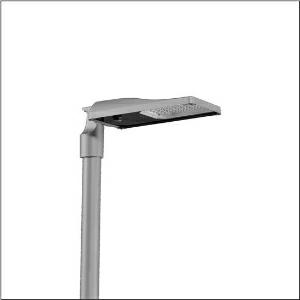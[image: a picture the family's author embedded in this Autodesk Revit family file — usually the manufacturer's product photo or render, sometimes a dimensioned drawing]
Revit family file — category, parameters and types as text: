
# Revit family: streetlight_sl_31_mini___st1_0a_5xh6d3ar08ga_0704
name_source: partatom
category: Lighting Fixtures
units: mm (PartAtom-declared; Revit-internal decimal feet)

## family parameters
Cut with Voids When Loaded = No
Host = Face
Light Source = No
Part Type = Normal
Room Calculation Point = No
Round Connector Dimension = Use Diameter
Shared = No

## types (1)
- --- (1 x LED, 5880 lm, 39.3 W, 3000K)
    Apparent Load = 39 VA
    CIE Flux Codes = 37 72 97 100 100
    Color Rendering = 70
    Color Temperature = 3000K
    Default Elevation = 1800 mm
    Description = Streetlight SL 31 mini D4i mast luminaire for post-top, side-entry; light control with lens of PMMA; light distribution: ST1.0a, direct asymmetric distribution, for standard-compliant lighting for roads and squares; LED: luminous flux: 5.880lm, light colour: 730, colour temperature: 3000K; luminous efficacy: 149,6lm/W; control: pre-setting: logarithmic dimming characteristic, flexible luminous flux parameterisation, time-dependent luminous flux control, constant luminous flux control, power reduction, intelligent temperature release in ECG and LED module, overheat protection; luminaire housing, of diecast aluminium, SITECO metallic grey (DB 702S), corrosivity category C5 high according to DIN EN ISO 12944; cover of toughened safety glass, transparent, opened without tools; mast flange of diecast aluminium, SITECO metallic grey (DB 702S), spigot size: 76/60mm, mast flange included unmounted; cable length: 6,5m, connection cable pre-assembled; mains connection: 220..240V, AC, 50/60Hz; power consumption (at start of service life): 39,3W / (at end of service life): 40,7W / (with reduced operation 50%): 18,1W; protection rating (complete): IP66; insulation class (complete): insulation class II (safety insulation); impact resistance: IK09; certification: CE, ENEC, ENEC+, VDE, UKCA, ZD4i; permissible operating ambient temperature for outdoor applications: -40..+50°C; packaging unit: 1 piece

Light Distribution: ST1.0a
    Height = 76 mm
    Lamp = 1 x LED
    Lamp Light Flux = 5880 lm
    Lamp Power = 39.3 W
    Lamp count = 1
    Length = 547 mm
    Luminous efficacy = 150 lm/W
    Manufacturer = Siteco
    ModVariant = No
    Model = 5XH6D3AR08GA
    Number of Poles = 1
    OnlyDefault = Yes
    Power Factor = 1
    Product Name = Streetlight SL 31 mini | ST1.0a
    Product group = mast luminaire | pylon top
    ProductGroupID = 6100
    Protection Class = Protection class II
    Protection Degree = IP 66
    RLX_Detail_Level = 1
    RLX_Emergency_Light_Flux = 0 lm
    RLX_Emergency_Type = 0
    RLX_Emergency_Type_DB = No
    RlxData = <blob elided: 39537 chars, md5=60c5152d>
    Socket = socket
    Standby Power = 0 W
    System Light Flux = 5880 lm
    System Power = 39 W
    Type Comments = factory setting: luminous flux: 100 % | dim-lin: 254 | 798 mA
    Type Image = l_1300328.jpg
    URL = http://relux.com
    VarID = @adj_060745
    Voltage = 0 V
    Weight = 0.00 kg
    Width = 265 mm

## geometry (parser evidence)
native form markers: Blend x4, Sweep x11
no freeform markers — native parametric forms only
